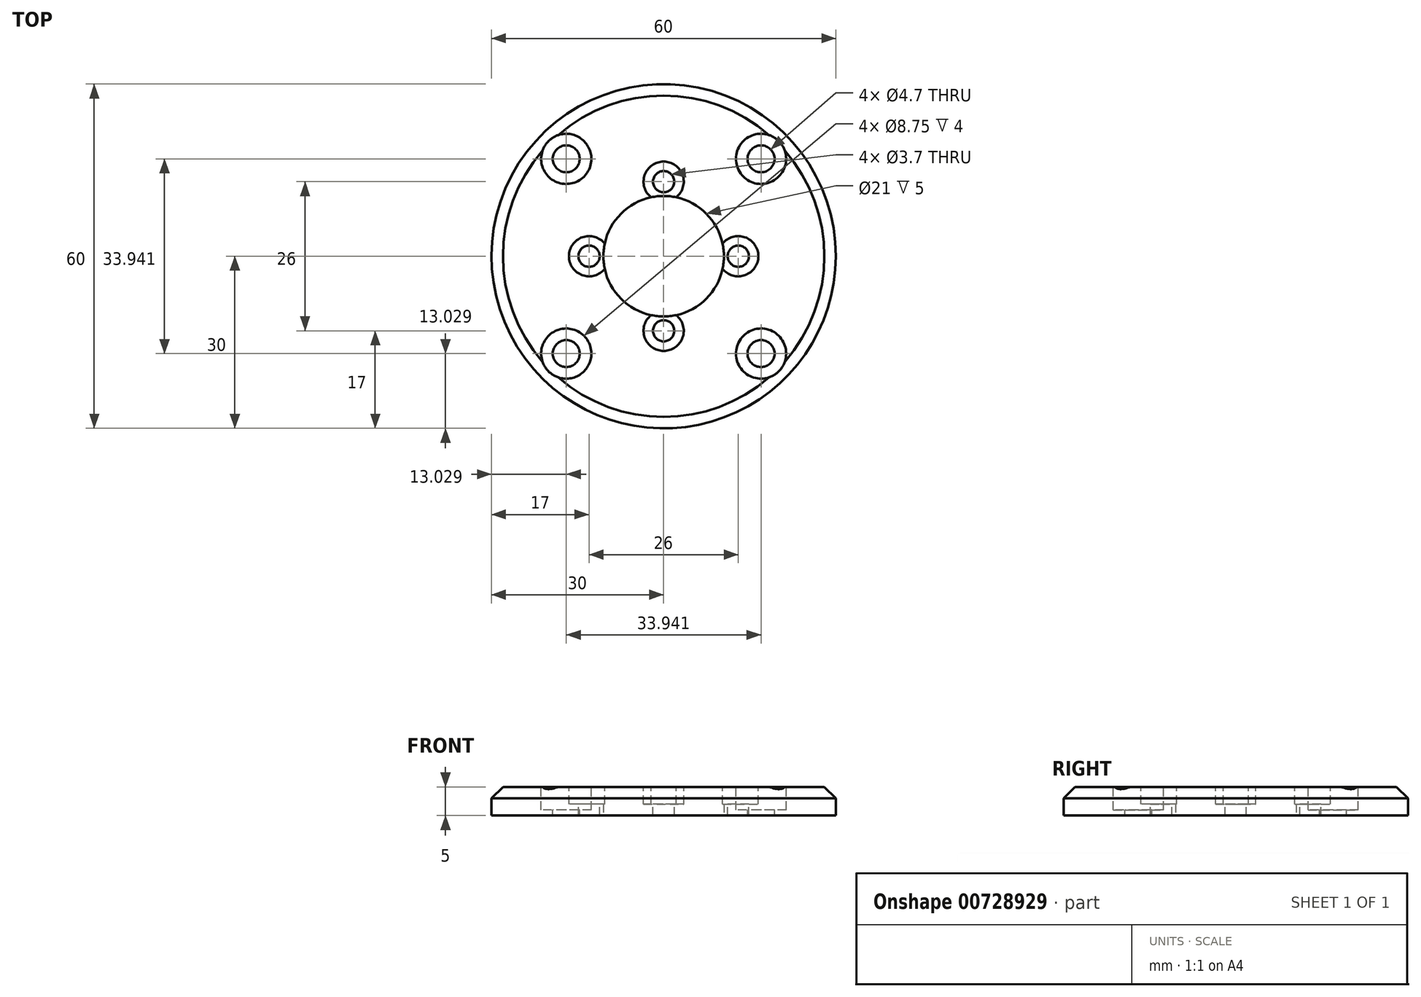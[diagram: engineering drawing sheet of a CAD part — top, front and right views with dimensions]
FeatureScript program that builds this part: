
annotation { "Feature Type Name" : "Feature", "Feature Type Description" : "" }
export const myFeature = defineFeature(function(context is Context, id is Id, definition is map)
    precondition{}
    {
        {
            var Q0;
            Q0=qCreatedBy(makeId("Top.planeOp"),FACE);
            var sketch = newSketch(context, id + "F0", { "sketchPlane" : qUnion([Q0])});
            skCircle(sketch, "E0", {"center": v(0, 0) * mm, "radius": 30 * mm});
            skCircle(sketch, "E1", {"center": v(0, 0) * mm, "radius": 10.5 * mm});
            skSolve(sketch);
        }
        {
            var Q0;
            Q0 = qSketchRegion(id + "F0", true);
            extrude(context, id + "F1", {"entities" : qUnion([Q0]), "depth" : 5 * mm, "offsetDistance" : 25 * mm});
        }
        {
            var Q0;
            Q0=makeQuery(id+"F1.opExtrude","CAP_FACE",FACE,{"disambiguationData":[OSD([sQuery(id+"F0.wireOp",EDGE,"E0"),sQuery(id+"F0.wireOp",EDGE,"E1")])],"isStart":false});
            var sketch = newSketch(context, id + "F2", { "sketchPlane" : qUnion([Q0])});
            skLineSegment(sketch, "E2.bottom", {"start": v(-16.97, 16.97) * mm, "end": v(16.97, 16.97) * mm, "construction": true});
            skLineSegment(sketch, "E2.top", {"start": v(-16.97, -16.97) * mm, "end": v(16.97, -16.97) * mm, "construction": true});
            skLineSegment(sketch, "E2.left", {"start": v(-16.97, 16.97) * mm, "end": v(-16.97, -16.97) * mm, "construction": true});
            skLineSegment(sketch, "E2.right", {"start": v(16.97, 16.97) * mm, "end": v(16.97, -16.97) * mm, "construction": true});
            skCircle(sketch, "E3", {"center": v(0, 0) * mm, "radius": 24 * mm, "construction": true});
            skSolve(sketch);
        }
        {
            var Q0;
            Q0=sQuery(id+"F2.wireOp",VERTEX,"E2.left.start");
            var Q1;
            Q1=sQuery(id+"F2.wireOp",VERTEX,"E2.right.start");
            var Q2;
            Q2=sQuery(id+"F2.wireOp",VERTEX,"E2.top.end");
            var Q3;
            Q3=sQuery(id+"F2.wireOp",VERTEX,"E2.left.end");
            var Q4;
            Q4=makeQuery(id+"F1.opExtrude","SWEPT_BODY",BODY,{"disambiguationData":[OSD([sQuery(id+"F0.wireOp",EDGE,"E0"),sQuery(id+"F0.wireOp",EDGE,"E1")])]});
            hole(context, id + "F3", {"style" : HoleStyle.C_BORE, "endStyle" : HoleEndStyle.THROUGH, "holeDiameter" : 4.7 * mm, "cBoreDiameter" : 8.75 * mm, "cBoreDepth" : 4 * mm, "majorDiameter" : 5 * mm, "isTappedThrough" : true, "tappedDepth" : 12 * mm, "tapClearance" : 3, "startFromSketch" : true, "locations" : qUnion([Q0, Q1, Q2, Q3]), "scope" : qUnion([Q4])});
        }
        {
            var Q0;
            Q0=makeQuery(id+"F1.opExtrude","CAP_FACE",FACE,{"disambiguationData":[OSD([sQuery(id+"F0.wireOp",EDGE,"E0"),sQuery(id+"F0.wireOp",EDGE,"E1")])],"isStart":false});
            var sketch = newSketch(context, id + "F4", { "sketchPlane" : qUnion([Q0])});
            skCircle(sketch, "E4.cCircle", {"center": v(0, 0) * mm, "radius": 13 * mm, "construction": true});
            skLineSegment(sketch, "E4.0", {"start": v(0, 13) * mm, "end": v(13, 0) * mm, "construction": true});
            skLineSegment(sketch, "E4.1", {"start": v(13, 0) * mm, "end": v(0, -13) * mm, "construction": true});
            skLineSegment(sketch, "E4.2", {"start": v(0, -13) * mm, "end": v(-13, 0) * mm, "construction": true});
            skLineSegment(sketch, "E4.3", {"start": v(-13, 0) * mm, "end": v(0, 13) * mm, "construction": true});
            skLineSegment(sketch, "E5", {"start": v(0, 0) * mm, "end": v(0, 13) * mm, "construction": true});
            skSolve(sketch);
        }
        {
            var Q0;
            Q0=sQuery(id+"F4.wireOp",VERTEX,"E4.0.start");
            var Q1;
            Q1=sQuery(id+"F4.wireOp",VERTEX,"E4.3.start");
            var Q2;
            Q2=sQuery(id+"F4.wireOp",VERTEX,"E4.2.start");
            var Q3;
            Q3=sQuery(id+"F4.wireOp",VERTEX,"E4.1.start");
            var Q4;
            Q4=makeQuery(id+"F1.opExtrude","SWEPT_BODY",BODY,{"disambiguationData":[OSD([sQuery(id+"F0.wireOp",EDGE,"E0"),sQuery(id+"F0.wireOp",EDGE,"E1")])]});
            hole(context, id + "F5", {"style" : HoleStyle.C_BORE, "endStyle" : HoleEndStyle.THROUGH, "holeDiameter" : 3.7 * mm, "cBoreDiameter" : 7 * mm, "cBoreDepth" : 3 * mm, "majorDiameter" : 5 * mm, "isTappedThrough" : true, "tappedDepth" : 12 * mm, "tapClearance" : 3, "startFromSketch" : true, "locations" : qUnion([Q0, Q1, Q2, Q3]), "scope" : qUnion([Q4])});
        }
        {
            var Q0;
            Q0=makeQuery(id+"F1.opExtrude","CAP_EDGE",EDGE,{"disambiguationData":[OSD([sQuery(id+"F0.wireOp",EDGE,"E0")])],"isStart":false});
            chamfer(context, id + "F6", {"entities" : qUnion([Q0]), "width" : 2 * mm, "tangentPropagation" : true});
        }
    });
